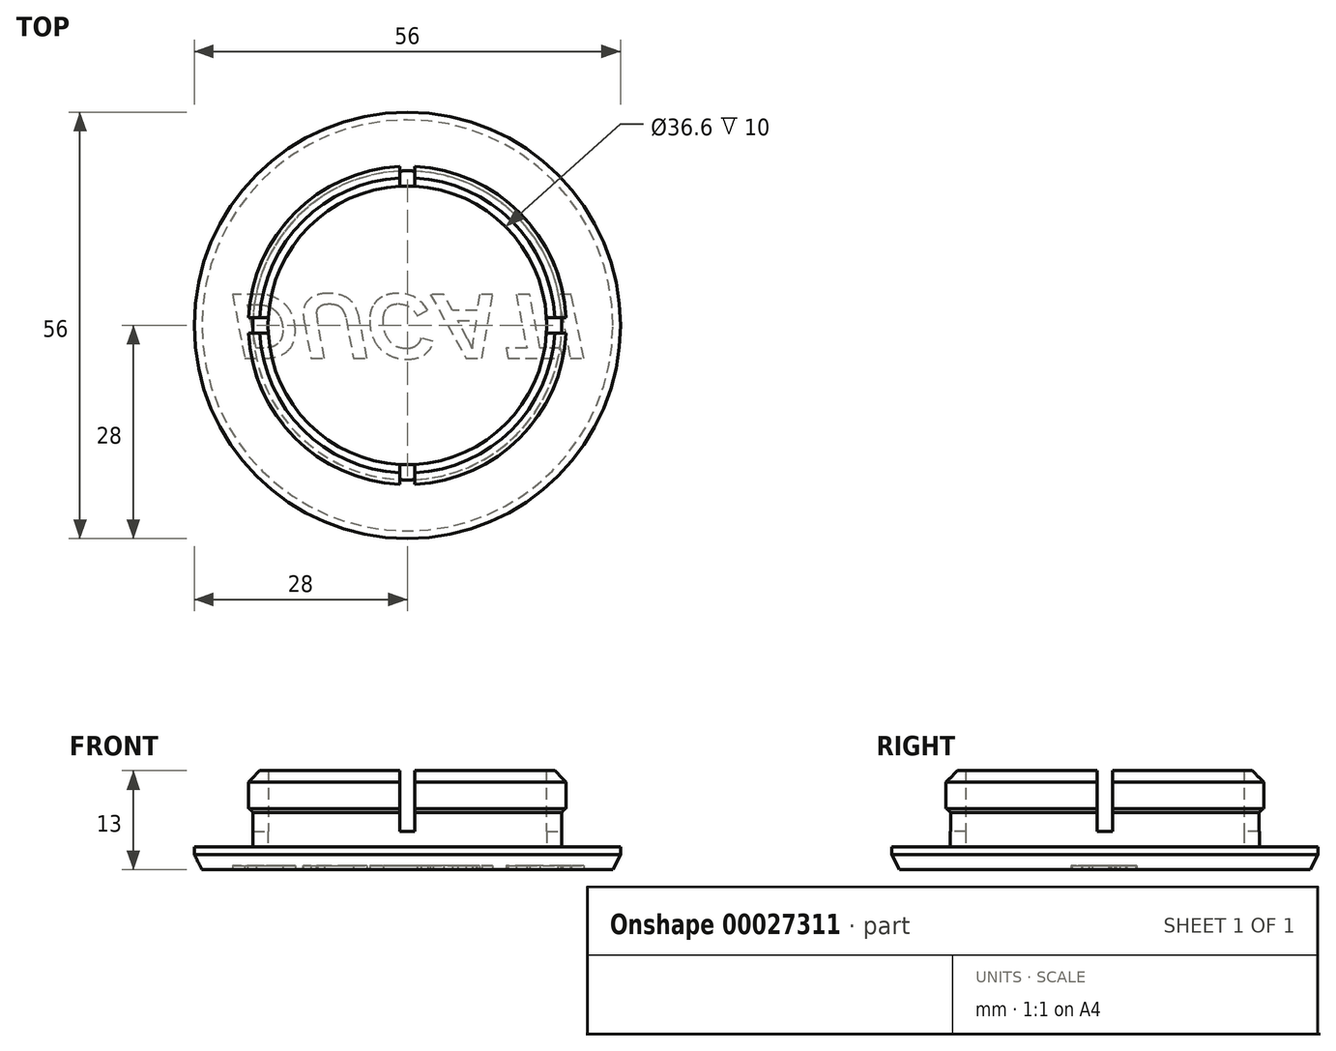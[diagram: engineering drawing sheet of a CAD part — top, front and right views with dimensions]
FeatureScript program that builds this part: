
annotation { "Feature Type Name" : "Feature", "Feature Type Description" : "" }
export const myFeature = defineFeature(function(context is Context, id is Id, definition is map)
    precondition{}
    {
        {
            var Q0;
            Q0=qCreatedBy(makeId("Top.planeOp"),FACE);
            var sketch = newSketch(context, id + "F0", { "sketchPlane" : qUnion([Q0])});
            skCircle(sketch, "E0", {"center": v(0, 0) * mm, "radius": 18.3 * mm});
            skCircle(sketch, "E1", {"center": v(0, 0) * mm, "radius": 20.3 * mm});
            skSolve(sketch);
        }
        {
            var Q0;
            Q0=qSketchRegion(id+"F0",true);
            extrude(context, id + "F1", {"entities" : qUnion([Q0]), "depth" : 10 * mm});
        }
        {
            var Q0;
            Q0=makeQuery(id+"F1.opExtrude","CAP_FACE",FACE,{"disambiguationData":[OSD([sQuery(id+"F0.wireOp",EDGE,"E0"),sQuery(id+"F0.wireOp",EDGE,"E1")])],"isStart":false});
            var sketch = newSketch(context, id + "F2", { "sketchPlane" : qUnion([Q0])});
            skCircle(sketch, "E2", {"center": v(0, 0) * mm, "radius": 18.3 * mm});
            skCircle(sketch, "E3", {"center": v(0, 0) * mm, "radius": 20.9 * mm});
            skSolve(sketch);
        }
        {
            var Q0;
            Q0=qSketchRegion(id+"F2",true);
            extrude(context, id + "F3", {"entities" : qUnion([Q0]), "operationType" : NewBodyOperationType.ADD, "oppositeDirection" : true, "depth" : 5 * mm});
        }
        {
            var Q0;
            Q0=makeQuery(id+"F3.opExtrude","CAP_EDGE",EDGE,{"disambiguationData":[OSD([sQuery(id+"F2.wireOp",EDGE,"E3")])],"isStart":true});
            chamfer(context, id + "F4", {"entities" : qUnion([Q0]), "width" : 1.5 * mm, "tangentPropagation" : true});
        }
        {
            var Q0;
            Q0=makeQuery(id+"F3.boolean.opBoolean","MERGE",FACE,{"derivedFrom":[makeQuery(id+"F1.opExtrude","CAP_FACE",FACE,{"disambiguationData":[OSD([sQuery(id+"F0.wireOp",EDGE,"E0"),sQuery(id+"F0.wireOp",EDGE,"E1")])],"isStart":false}),makeQuery(id+"F3.opExtrude","CAP_FACE",FACE,{"disambiguationData":[OSD([sQuery(id+"F2.wireOp",EDGE,"E2"),sQuery(id+"F2.wireOp",EDGE,"E3")])],"isStart":true})]});
            var sketch = newSketch(context, id + "F5", { "sketchPlane" : qUnion([Q0])});
            skLineSegment(sketch, "E4.bottom", {"start": v(-1, 25) * mm, "end": v(1, 25) * mm});
            skLineSegment(sketch, "E4.top", {"start": v(-1, -25) * mm, "end": v(1, -25) * mm});
            skLineSegment(sketch, "E4.left", {"start": v(-1, 25) * mm, "end": v(-1, -25) * mm});
            skLineSegment(sketch, "E4.right", {"start": v(1, 25) * mm, "end": v(1, -25) * mm});
            skLineSegment(sketch, "E5.bottom", {"start": v(-25, 1) * mm, "end": v(25, 1) * mm});
            skLineSegment(sketch, "E5.top", {"start": v(-25, -1) * mm, "end": v(25, -1) * mm});
            skLineSegment(sketch, "E5.left", {"start": v(-25, 1) * mm, "end": v(-25, -1) * mm});
            skLineSegment(sketch, "E5.right", {"start": v(25, 1) * mm, "end": v(25, -1) * mm});
            skSolve(sketch);
        }
        {
            var Q0;
            Q0=qSketchRegion(id+"F5",true);
            extrude(context, id + "F6", {"entities" : qUnion([Q0]), "operationType" : NewBodyOperationType.REMOVE, "oppositeDirection" : true, "depth" : 8 * mm});
        }
        {
            var Q0;
            Q0=makeQuery(id+"F1.opExtrude","CAP_FACE",FACE,{"disambiguationData":[OSD([sQuery(id+"F0.wireOp",EDGE,"E0"),sQuery(id+"F0.wireOp",EDGE,"E1")])],"isStart":true});
            var sketch = newSketch(context, id + "F7", { "sketchPlane" : qUnion([Q0])});
            skCircle(sketch, "E6", {"center": v(0, 0) * mm, "radius": 28 * mm});
            skSolve(sketch);
        }
        {
            var Q0;
            Q0=qSketchRegion(id+"F7",true);
            extrude(context, id + "F8", {"entities" : qUnion([Q0]), "operationType" : NewBodyOperationType.ADD, "depth" : 3 * mm});
        }
        {
            var Q0;
            Q0=makeQuery(id+"F8.opExtrude","CAP_EDGE",EDGE,{"disambiguationData":[OSD([sQuery(id+"F7.wireOp",EDGE,"E6")])],"isStart":false});
            chamfer(context, id + "F9", {"entities" : qUnion([Q0]), "chamferType" : ChamferType.TWO_OFFSETS, "width1" : 1 * mm, "oppositeDirection" : false, "width2" : 2 * mm, "tangentPropagation" : true});
        }
        {
            var Q0;
            {var subQ0=sQuery(id+"F0.wireOp",EDGE,"E1");var subQ1=makeQuery(id+"F1.opExtrude","SWEPT_FACE",FACE,{"disambiguationData":[OSD([subQ0])]});var subQ2=sQuery(id+"F2.wireOp",EDGE,"E2");var subQ3=sQuery(id+"F2.wireOp",EDGE,"E3");var subQ4=makeQuery(id+"F3.opExtrude","CAP_FACE",FACE,{"disambiguationData":[OSD([subQ2,subQ3])],"isStart":false});var subQ5=sQuery(id+"F5.wireOp",EDGE,"E5.top");var subQ6=sQuery(id+"F0.wireOp",EDGE,"E0");var subQ7=makeQuery(id+"F1.opExtrude","CAP_EDGE",EDGE,{"disambiguationData":[OSD([subQ6])],"isStart":false});var subQ9=sQuery(id+"F5.wireOp",EDGE,"E4.right");var subQ10=makeQuery(id+"F5.imprint","INTERSECT",VERTEX,{"derivedFrom":[subQ9,subQ5]});var subQ13=makeQuery(id+"F5.imprint","INTERSECT",VERTEX,{"disambiguationData":[OD(1.0)],"derivedFrom":[subQ7,subQ9]});Q0=makeQuery(id+"F6.boolean.opBoolean","SPLIT",EDGE,{"disambiguationData":[TD([makeQuery(id+"F6.opExtrude","SWEPT_FACE",FACE,{"disambiguationData":[OSD([subQ9]),TDD([makeQuery(id+"F5.imprint","IMPRINT",EDGE,{"disambiguationData":[TD([[subQ10,-1.0]])],"derivedFrom":subQ9}),makeQuery(id+"F5.imprint","IMPRINT",EDGE,{"disambiguationData":[TD([[subQ13,-1.0]])],"derivedFrom":subQ9}),makeQuery(id+"F5.imprint","IMPRINT",EDGE,{"disambiguationData":[TD([[makeQuery(id+"F5.imprint","INTERSECT",VERTEX,{"derivedFrom":[sQuery(id+"F5.wireOp",EDGE,"E4.top"),subQ9]}),1.0]])],"derivedFrom":subQ9})])]})])],"derivedFrom":makeQuery(id+"F3.boolean.opBoolean","INTERSECT",EDGE,{"derivedFrom":[subQ1,subQ4]})});}
            var Q1;
            {var subQ0=sQuery(id+"F0.wireOp",EDGE,"E1");var subQ1=makeQuery(id+"F1.opExtrude","SWEPT_FACE",FACE,{"disambiguationData":[OSD([subQ0])]});var subQ2=sQuery(id+"F2.wireOp",EDGE,"E2");var subQ3=sQuery(id+"F2.wireOp",EDGE,"E3");var subQ4=makeQuery(id+"F3.opExtrude","CAP_FACE",FACE,{"disambiguationData":[OSD([subQ2,subQ3])],"isStart":false});var subQ5=sQuery(id+"F5.wireOp",EDGE,"E5.bottom");var subQ6=sQuery(id+"F0.wireOp",EDGE,"E0");var subQ7=makeQuery(id+"F1.opExtrude","CAP_EDGE",EDGE,{"disambiguationData":[OSD([subQ6])],"isStart":false});var subQ9=sQuery(id+"F5.wireOp",EDGE,"E4.right");var subQ10=makeQuery(id+"F5.imprint","INTERSECT",VERTEX,{"derivedFrom":[subQ9,subQ5]});var subQ14=makeQuery(id+"F5.imprint","INTERSECT",VERTEX,{"disambiguationData":[OD(0.0)],"derivedFrom":[subQ7,subQ9]});Q1=makeQuery(id+"F6.boolean.opBoolean","SPLIT",EDGE,{"disambiguationData":[TD([makeQuery(id+"F6.opExtrude","SWEPT_FACE",FACE,{"disambiguationData":[OSD([subQ9]),TDD([makeQuery(id+"F5.imprint","IMPRINT",EDGE,{"disambiguationData":[TD([[makeQuery(id+"F5.imprint","INTERSECT",VERTEX,{"derivedFrom":[sQuery(id+"F5.wireOp",EDGE,"E4.bottom"),subQ9]}),-1.0]])],"derivedFrom":subQ9}),makeQuery(id+"F5.imprint","IMPRINT",EDGE,{"disambiguationData":[TD([[subQ14,1.0]])],"derivedFrom":subQ9}),makeQuery(id+"F5.imprint","IMPRINT",EDGE,{"disambiguationData":[TD([[subQ10,1.0]])],"derivedFrom":subQ9})])]})])],"derivedFrom":makeQuery(id+"F3.boolean.opBoolean","INTERSECT",EDGE,{"derivedFrom":[subQ1,subQ4]})});}
            var Q2;
            {var subQ0=sQuery(id+"F0.wireOp",EDGE,"E1");var subQ1=makeQuery(id+"F1.opExtrude","SWEPT_FACE",FACE,{"disambiguationData":[OSD([subQ0])]});var subQ2=sQuery(id+"F2.wireOp",EDGE,"E2");var subQ3=sQuery(id+"F2.wireOp",EDGE,"E3");var subQ4=makeQuery(id+"F3.opExtrude","CAP_FACE",FACE,{"disambiguationData":[OSD([subQ2,subQ3])],"isStart":false});var subQ5=sQuery(id+"F5.wireOp",EDGE,"E5.top");var subQ6=sQuery(id+"F0.wireOp",EDGE,"E0");var subQ9=makeQuery(id+"F1.opExtrude","CAP_EDGE",EDGE,{"disambiguationData":[OSD([subQ6])],"isStart":false});var subQ11=sQuery(id+"F5.wireOp",EDGE,"E4.left");var subQ12=makeQuery(id+"F5.imprint","INTERSECT",VERTEX,{"derivedFrom":[subQ11,subQ5]});var subQ13=makeQuery(id+"F5.imprint","INTERSECT",VERTEX,{"disambiguationData":[OD(1.0)],"derivedFrom":[subQ9,subQ11]});Q2=makeQuery(id+"F6.boolean.opBoolean","SPLIT",EDGE,{"disambiguationData":[TD([makeQuery(id+"F6.opExtrude","SWEPT_FACE",FACE,{"disambiguationData":[OSD([subQ11]),TDD([makeQuery(id+"F5.imprint","IMPRINT",EDGE,{"disambiguationData":[TD([[subQ12,-1.0]])],"derivedFrom":subQ11}),makeQuery(id+"F5.imprint","IMPRINT",EDGE,{"disambiguationData":[TD([[subQ13,-1.0]])],"derivedFrom":subQ11}),makeQuery(id+"F5.imprint","IMPRINT",EDGE,{"disambiguationData":[TD([[makeQuery(id+"F5.imprint","INTERSECT",VERTEX,{"derivedFrom":[sQuery(id+"F5.wireOp",EDGE,"E4.top"),subQ11]}),1.0]])],"derivedFrom":subQ11})])]})])],"derivedFrom":makeQuery(id+"F3.boolean.opBoolean","INTERSECT",EDGE,{"derivedFrom":[subQ1,subQ4]})});}
            var Q3;
            {var subQ0=sQuery(id+"F0.wireOp",EDGE,"E1");var subQ1=makeQuery(id+"F1.opExtrude","SWEPT_FACE",FACE,{"disambiguationData":[OSD([subQ0])]});var subQ2=sQuery(id+"F2.wireOp",EDGE,"E2");var subQ3=sQuery(id+"F2.wireOp",EDGE,"E3");var subQ4=makeQuery(id+"F3.opExtrude","CAP_FACE",FACE,{"disambiguationData":[OSD([subQ2,subQ3])],"isStart":false});var subQ5=sQuery(id+"F5.wireOp",EDGE,"E5.bottom");var subQ6=sQuery(id+"F0.wireOp",EDGE,"E0");var subQ9=makeQuery(id+"F1.opExtrude","CAP_EDGE",EDGE,{"disambiguationData":[OSD([subQ6])],"isStart":false});var subQ11=sQuery(id+"F5.wireOp",EDGE,"E4.left");var subQ12=makeQuery(id+"F5.imprint","INTERSECT",VERTEX,{"derivedFrom":[subQ11,subQ5]});var subQ14=makeQuery(id+"F5.imprint","INTERSECT",VERTEX,{"disambiguationData":[OD(0.0)],"derivedFrom":[subQ9,subQ11]});Q3=makeQuery(id+"F6.boolean.opBoolean","SPLIT",EDGE,{"disambiguationData":[TD([makeQuery(id+"F6.opExtrude","SWEPT_FACE",FACE,{"disambiguationData":[OSD([subQ11]),TDD([makeQuery(id+"F5.imprint","IMPRINT",EDGE,{"disambiguationData":[TD([[makeQuery(id+"F5.imprint","INTERSECT",VERTEX,{"derivedFrom":[sQuery(id+"F5.wireOp",EDGE,"E4.bottom"),subQ11]}),-1.0]])],"derivedFrom":subQ11}),makeQuery(id+"F5.imprint","IMPRINT",EDGE,{"disambiguationData":[TD([[subQ14,1.0]])],"derivedFrom":subQ11}),makeQuery(id+"F5.imprint","IMPRINT",EDGE,{"disambiguationData":[TD([[subQ12,1.0]])],"derivedFrom":subQ11})])]})])],"derivedFrom":makeQuery(id+"F3.boolean.opBoolean","INTERSECT",EDGE,{"derivedFrom":[subQ1,subQ4]})});}
            chamfer(context, id + "F10", {"entities" : qUnion([Q0, Q1, Q2, Q3]), "width" : .5 * mm, "tangentPropagation" : true});
        }
        {
            var Q0;
            Q0=makeQuery(id+"F8.opExtrude","CAP_FACE",FACE,{"disambiguationData":[OSD([sQuery(id+"F7.wireOp",EDGE,"E6")])],"isStart":false});
            var sketch = newSketch(context, id + "F11", { "sketchPlane" : qUnion([Q0])});
            skText(sketch, "E7", { "text": "DUCATI", "fontName": "Arimo-BoldItalic.ttf"});
            const initialGuessF11  = {"E7": [-0.0232, -0.00409, 1, 0, 0.0088]};
            skSetInitialGuess(sketch, initialGuessF11);
            skSolve(sketch);
        }
        {
            var Q0;
            Q0=makeQuery(id+"F11.imprint","IMPRINT",FACE,{"disambiguationData":[TD([[makeQuery(id+"F11.imprint","IMPRINT",EDGE,{"derivedFrom":sQuery(id+"F11.wireOp",EDGE,"E7.sketch_text.stroke-16")}),-1.0]])]});
            var Q1;
            Q1=makeQuery(id+"F11.imprint","IMPRINT",FACE,{"disambiguationData":[TD([[makeQuery(id+"F11.imprint","IMPRINT",EDGE,{"derivedFrom":sQuery(id+"F11.wireOp",EDGE,"E7.sketch_text.stroke-33")}),-1.0]])]});
            var Q2;
            Q2=makeQuery(id+"F11.imprint","IMPRINT",FACE,{"disambiguationData":[TD([[makeQuery(id+"F11.imprint","IMPRINT",EDGE,{"derivedFrom":sQuery(id+"F11.wireOp",EDGE,"E7.sketch_text.stroke-64")}),-1.0]])]});
            var Q3;
            Q3=makeQuery(id+"F11.imprint","IMPRINT",FACE,{"disambiguationData":[TD([[makeQuery(id+"F11.imprint","IMPRINT",EDGE,{"derivedFrom":sQuery(id+"F11.wireOp",EDGE,"E7.sketch_text.stroke-72")}),-1.0]])]});
            var Q4;
            Q4=makeQuery(id+"F11.imprint","IMPRINT",FACE,{"disambiguationData":[TD([[makeQuery(id+"F11.imprint","IMPRINT",EDGE,{"derivedFrom":sQuery(id+"F11.wireOp",EDGE,"E7.sketch_text.stroke-0")}),-1.0]])]});
            var Q5;
            Q5=makeQuery(id+"F11.imprint","IMPRINT",FACE,{"disambiguationData":[TD([[makeQuery(id+"F11.imprint","IMPRINT",EDGE,{"derivedFrom":sQuery(id+"F11.wireOp",EDGE,"E7.sketch_text.stroke-51")}),-1.0]])]});
            extrude(context, id + "F12", {"entities" : qUnion([Q0, Q1, Q2, Q3, Q4, Q5]), "operationType" : NewBodyOperationType.REMOVE, "oppositeDirection" : true, "depth" : .5 * mm});
        }
    });
